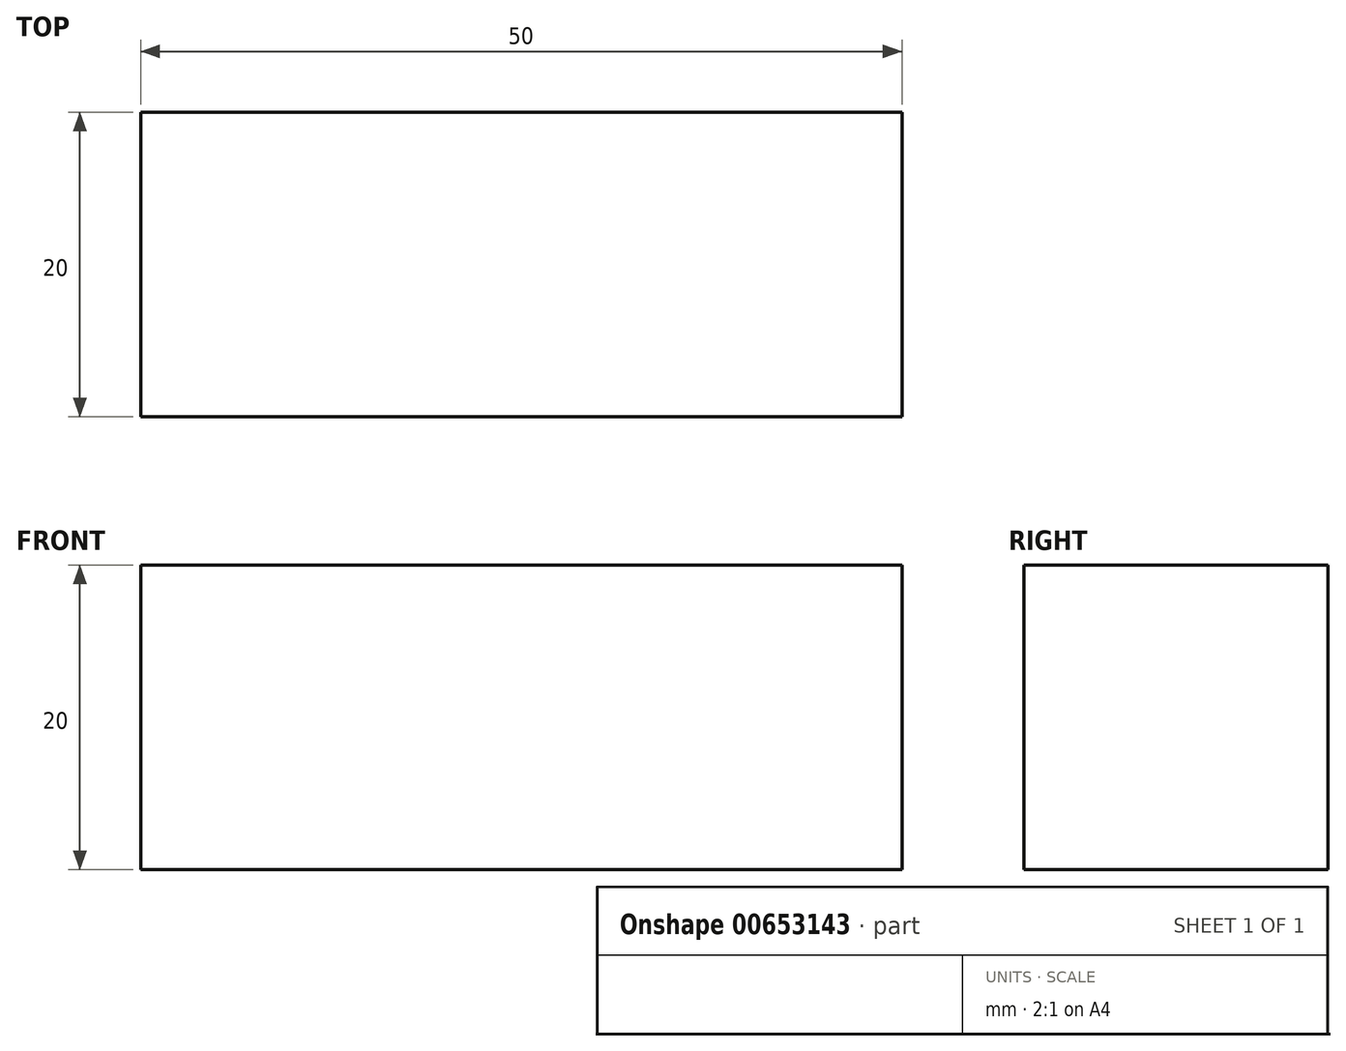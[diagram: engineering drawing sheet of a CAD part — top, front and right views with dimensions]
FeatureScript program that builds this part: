
annotation { "Feature Type Name" : "Feature", "Feature Type Description" : "" }
export const myFeature = defineFeature(function(context is Context, id is Id, definition is map)
    precondition{}
    {
        {
            var Q0;
            Q0=qCreatedBy(makeId("Front.planeOp"),FACE);
            var sketch = newSketch(context, id + "F0", { "sketchPlane" : qUnion([Q0])});
            skLineSegment(sketch, "E0.bottom", {"start": v(25, 10) * mm, "end": v(-25, 10) * mm});
            skLineSegment(sketch, "E0.top", {"start": v(25, -10) * mm, "end": v(-25, -10) * mm});
            skLineSegment(sketch, "E0.left", {"start": v(25, 10) * mm, "end": v(25, -10) * mm});
            skLineSegment(sketch, "E0.right", {"start": v(-25, 10) * mm, "end": v(-25, -10) * mm});
            skPoint(sketch, "E0.middle", {"position": v(0, 0) * mm});
            skSolve(sketch);
        }
        {
            var Q0;
            Q0=makeQuery(id+"F0.imprint","IMPRINT",FACE,{"disambiguationData":[TD([[makeQuery(id+"F0.imprint","IMPRINT",EDGE,{"derivedFrom":sQuery(id+"F0.wireOp",EDGE,"E0.bottom")}),1.0]])]});
            extrude(context, id + "F1", {"entities" : qUnion([Q0]), "depth" : 20 * mm, "offsetDistance" : 25 * mm});
        }
    });
